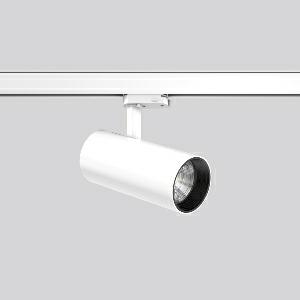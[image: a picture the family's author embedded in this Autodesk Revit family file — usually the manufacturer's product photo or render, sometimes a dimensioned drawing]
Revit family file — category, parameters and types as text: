
# Revit family: deecos_s_mini_742198_002_9701
name_source: partatom
category: Lighting Fixtures
units: mm (PartAtom-declared; Revit-internal decimal feet)

## family parameters
Cut with Voids When Loaded = No
Host = Face
Light Source = No
Part Type = Normal
Room Calculation Point = No
Round Connector Dimension = Use Diameter
Shared = No

## types (1)
- DEECOS S mini (1 x LED Modul 930, 2250 lm, 3000)
    Apparent Load = 20 VA
    Approval mark = CE
    CIE Flux Codes = 99 100 100 100 100
    Color Rendering = 90
    Color Temperature = 3000
    Default Elevation = 1800 mm
    Description = Series: DEECOS S mini
LED surface-mounted projector in modern design with no visible cooling ribs. Housing: die-cast aluminium, powder-coated. Rotation range: 356°. Swivel range: 90°. Black plastic ring and recessed LED to prevent glare from the side. Optical assembly with lens made of plastic (polycarbonate) for the best homogeneous light distribution - can be changed without tools. Best colour rendering index Ra>90. With multi adaptor for 3-circuit tracks 230 V. Suitable for Track on ceiling, Wall track. High quality converter without flickering and stroboscopic effect. The following accessories can be mounted without use of tools: interchangeable lenses, decorative glasses, honeycomb louvre, clear and frosted diffusers, white interchangeable plastic ring. 
Colour: traffic white, matt (RAL 9016)
Diameter: 87 mm
Height: 214 mm
Lamp: LED
Socket: without socket
Colour temperature: 3000K
Colour rendering index (CRI): 92
System power: 20 W
Rated luminous flux: 2250 lm
Luminous efficiency: 113 lm/W
Control gear: Regulated power supply
Protection class: I
Type of protection: IP 20
    Height = 214 mm
    Lamp = 1 x LED Modul 930
    Lamp Light Flux = 2250 lm
    Lamp count = 1
    Length = 87 mm
    Lifetime = 50000 h
    Luminous efficacy = 113 lm/W
    Manufacturer = RZB
    ModVariant = No
    Model = 742198.002
    Mounting Place = Ceiling
    Mounting Type = Rail mounted
    Number of Poles = 1
    OnlyDefault = Yes
    Power Factor = 1
    Product Name = DEECOS S mini
    Product group = Track mounted projectors
    ProductGroupID = 301
    Protection Class = Protection class I
    Protection Degree = IP 20
    RLX_Detail_Level = 1
    RLX_Emergency_Light_Flux = 0 lm
    RLX_Emergency_Type = 0
    RLX_Emergency_Type_DB = No
    RlxData = <blob elided: 35221 chars, md5=82de3857>
    Socket = socket
    Standby Power = 0 W
    System Light Flux = 2250 lm
    System Power = 20 W
    Type Comments = Product without accessories
    Type Image = 741930.002.jpg
    URL = http://relux.com
    VarID = ---
    Voltage = 230 V
    Voltage Range = 220-240 V
    Weight = 0.00 kg
    Width = 0 mm  [stored 0 ft]

note: [stored X ft] marks values corroborated as IEEE doubles in the binary element streams (Revit-internal decimal feet)

## geometry (parser evidence)
native form markers: Blend x4, Sweep x12
no freeform markers — native parametric forms only
